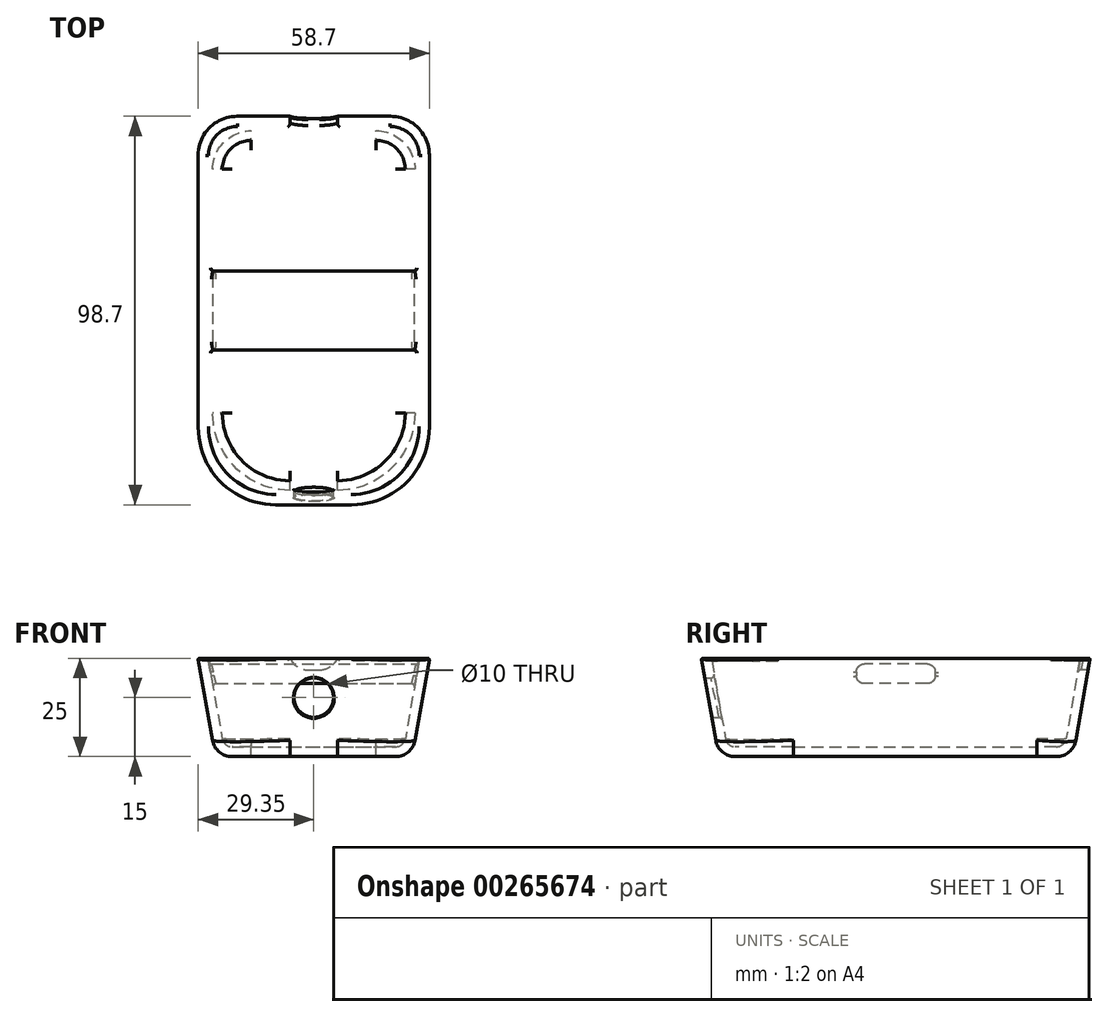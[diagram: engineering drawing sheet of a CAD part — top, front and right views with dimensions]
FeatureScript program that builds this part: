
annotation { "Feature Type Name" : "Feature", "Feature Type Description" : "" }
export const myFeature = defineFeature(function(context is Context, id is Id, definition is map)
    precondition{}
    {
        {
            var Q0;
            Q0=qCreatedBy(makeId("Top.planeOp"),FACE);
            var sketch = newSketch(context, id + "F0", { "sketchPlane" : qUnion([Q0])});
            skLineSegment(sketch, "E0.bottom", {"start": v(-25, 45) * mm, "end": v(25, 45) * mm});
            skLineSegment(sketch, "E0.top", {"start": v(-25, -45) * mm, "end": v(25, -45) * mm});
            skLineSegment(sketch, "E0.left", {"start": v(-25, 45) * mm, "end": v(-25, -45) * mm});
            skLineSegment(sketch, "E0.right", {"start": v(25, 45) * mm, "end": v(25, -45) * mm});
            skPoint(sketch, "E0.middle", {"position": v(0, 0) * mm});
            skSolve(sketch);
        }
        {
            var Q0;
            Q0=makeQuery(id+"F0.imprint","IMPRINT",FACE,{"disambiguationData":[TD([[makeQuery(id+"F0.imprint","IMPRINT",EDGE,{"derivedFrom":sQuery(id+"F0.wireOp",EDGE,"E0.bottom")}),-1.0]])]});
            extrude(context, id + "F1", {"entities" : qUnion([Q0]), "depth" : 25 * mm, "hasDraft" : true, "draftAngle" : 10 * degree});
        }
        {
            var Q0;
            Q0=makeQuery(id+"F1.opExtrude","SWEPT_EDGE",EDGE,{"disambiguationData":[OSD([sQuery(id+"F0.wireOp",EDGE,"E0.top"),sQuery(id+"F0.wireOp",EDGE,"E0.right")])]});
            var Q1;
            Q1=makeQuery(id+"F1.opExtrude","SWEPT_EDGE",EDGE,{"disambiguationData":[OSD([sQuery(id+"F0.wireOp",EDGE,"E0.top"),sQuery(id+"F0.wireOp",EDGE,"E0.left")])]});
            fillet(context, id + "F12", {"entities" : qUnion([Q0, Q1]), "radius" : 20 * mm, "tangentPropagation" : true, "allowEdgeOverflow" : false});
        }
        {
            var Q0;
            Q0=makeQuery(id+"F1.opExtrude","SWEPT_EDGE",EDGE,{"disambiguationData":[OSD([sQuery(id+"F0.wireOp",EDGE,"E0.bottom"),sQuery(id+"F0.wireOp",EDGE,"E0.left")])]});
            var Q1;
            Q1=makeQuery(id+"F1.opExtrude","SWEPT_EDGE",EDGE,{"disambiguationData":[OSD([sQuery(id+"F0.wireOp",EDGE,"E0.bottom"),sQuery(id+"F0.wireOp",EDGE,"E0.right")])]});
            fillet(context, id + "F2", {"entities" : qUnion([Q0, Q1]), "radius" : 10 * mm, "tangentPropagation" : true, "allowEdgeOverflow" : false});
        }
        {
            var Q0;
            Q0=makeQuery(id+"F1.opExtrude","CAP_EDGE",EDGE,{"disambiguationData":[OSD([sQuery(id+"F0.wireOp",EDGE,"E0.right")])],"isStart":true});
            var Q1;
            {var subQ0=sQuery(id+"F0.wireOp",EDGE,"E0.right");var subQ1=sQuery(id+"F0.wireOp",EDGE,"E0.bottom");Q1=makeQuery(id+"F2.opFillet","BLEND_EDGE",EDGE,{"blendedFrom":[makeQuery(id+"F1.opExtrude","SWEPT_EDGE",EDGE,{"disambiguationData":[OSD([subQ1,subQ0])]}),makeQuery(id+"F1.opExtrude","CAP_FACE",FACE,{"disambiguationData":[OSD([subQ1,sQuery(id+"F0.wireOp",EDGE,"E0.top"),sQuery(id+"F0.wireOp",EDGE,"E0.left"),subQ0])],"isStart":true})],"blendedInto":[makeQuery(id+"F1.opExtrude","CAP_FACE",FACE,{"disambiguationData":[OSD([subQ1,sQuery(id+"F0.wireOp",EDGE,"E0.top"),sQuery(id+"F0.wireOp",EDGE,"E0.left"),subQ0])],"isStart":true})]});}
            var Q2;
            Q2=makeQuery(id+"F1.opExtrude","CAP_EDGE",EDGE,{"disambiguationData":[OSD([sQuery(id+"F0.wireOp",EDGE,"E0.bottom")])],"isStart":true});
            var Q3;
            {var subQ0=sQuery(id+"F0.wireOp",EDGE,"E0.left");var subQ1=sQuery(id+"F0.wireOp",EDGE,"E0.bottom");Q3=makeQuery(id+"F2.opFillet","BLEND_EDGE",EDGE,{"blendedFrom":[makeQuery(id+"F1.opExtrude","SWEPT_EDGE",EDGE,{"disambiguationData":[OSD([subQ1,subQ0])]}),makeQuery(id+"F1.opExtrude","CAP_FACE",FACE,{"disambiguationData":[OSD([subQ1,sQuery(id+"F0.wireOp",EDGE,"E0.top"),subQ0,sQuery(id+"F0.wireOp",EDGE,"E0.right")])],"isStart":true})],"blendedInto":[makeQuery(id+"F1.opExtrude","CAP_FACE",FACE,{"disambiguationData":[OSD([subQ1,sQuery(id+"F0.wireOp",EDGE,"E0.top"),subQ0,sQuery(id+"F0.wireOp",EDGE,"E0.right")])],"isStart":true})]});}
            var Q4;
            Q4=makeQuery(id+"F1.opExtrude","CAP_EDGE",EDGE,{"disambiguationData":[OSD([sQuery(id+"F0.wireOp",EDGE,"E0.left")])],"isStart":true});
            var Q5;
            {var subQ0=sQuery(id+"F0.wireOp",EDGE,"E0.left");var subQ1=sQuery(id+"F0.wireOp",EDGE,"E0.top");Q5=makeQuery(id+"F12.opFillet","BLEND_EDGE",EDGE,{"blendedFrom":[makeQuery(id+"F1.opExtrude","SWEPT_EDGE",EDGE,{"disambiguationData":[OSD([subQ1,subQ0])]}),makeQuery(id+"F1.opExtrude","CAP_FACE",FACE,{"disambiguationData":[OSD([sQuery(id+"F0.wireOp",EDGE,"E0.bottom"),subQ1,subQ0,sQuery(id+"F0.wireOp",EDGE,"E0.right")])],"isStart":true})],"blendedInto":[makeQuery(id+"F1.opExtrude","CAP_FACE",FACE,{"disambiguationData":[OSD([sQuery(id+"F0.wireOp",EDGE,"E0.bottom"),subQ1,subQ0,sQuery(id+"F0.wireOp",EDGE,"E0.right")])],"isStart":true})]});}
            var Q6;
            {var subQ0=sQuery(id+"F0.wireOp",EDGE,"E0.right");var subQ1=sQuery(id+"F0.wireOp",EDGE,"E0.top");Q6=makeQuery(id+"F12.opFillet","BLEND_EDGE",EDGE,{"blendedFrom":[makeQuery(id+"F1.opExtrude","SWEPT_EDGE",EDGE,{"disambiguationData":[OSD([subQ1,subQ0])]}),makeQuery(id+"F1.opExtrude","CAP_FACE",FACE,{"disambiguationData":[OSD([sQuery(id+"F0.wireOp",EDGE,"E0.bottom"),subQ1,sQuery(id+"F0.wireOp",EDGE,"E0.left"),subQ0])],"isStart":true})],"blendedInto":[makeQuery(id+"F1.opExtrude","CAP_FACE",FACE,{"disambiguationData":[OSD([sQuery(id+"F0.wireOp",EDGE,"E0.bottom"),subQ1,sQuery(id+"F0.wireOp",EDGE,"E0.left"),subQ0])],"isStart":true})]});}
            var Q7;
            Q7=makeQuery(id+"F1.opExtrude","CAP_EDGE",EDGE,{"disambiguationData":[OSD([sQuery(id+"F0.wireOp",EDGE,"E0.top")])],"isStart":true});
            fillet(context, id + "F3", {"entities" : qUnion([Q0, Q1, Q2, Q3, Q4, Q5, Q6, Q7]), "radius" : 5 * mm, "tangentPropagation" : true, "allowEdgeOverflow" : false});
        }
        {
            var Q0;
            Q0=makeQuery(id+"F1.opExtrude","CAP_FACE",FACE,{"disambiguationData":[OSD([sQuery(id+"F0.wireOp",EDGE,"E0.bottom"),sQuery(id+"F0.wireOp",EDGE,"E0.top"),sQuery(id+"F0.wireOp",EDGE,"E0.left"),sQuery(id+"F0.wireOp",EDGE,"E0.right")])],"isStart":false});
            shell(context, id + "F4", {"entities" : qUnion([Q0]), "thickness" : 2.5 * mm});
        }
        {
            var Q0;
            Q0=qCreatedBy(makeId("Front.planeOp"),FACE);
            var sketch = newSketch(context, id + "F5", { "sketchPlane" : qUnion([Q0])});
            skLineSegment(sketch, "E1", {"start": v(0, 0) * mm, "end": v(0, 25) * mm, "construction": true});
            skLineSegment(sketch, "E2.bottom", {"start": v(9.5, 33.44) * mm, "end": v(10.2, 33.44) * mm});
            skLineSegment(sketch, "E2.top", {"start": v(9.5, 33.72) * mm, "end": v(10.2, 33.72) * mm});
            skLineSegment(sketch, "E2.left", {"start": v(9.5, 33.44) * mm, "end": v(9.5, 33.72) * mm});
            skLineSegment(sketch, "E2.right", {"start": v(10.2, 33.44) * mm, "end": v(10.2, 33.72) * mm});
            skPoint(sketch, "E2.middle", {"position": v(9.85, 33.58) * mm});
            skLineSegment(sketch, "E3.bottom", {"start": v(6, 28) * mm, "end": v(-6, 28) * mm});
            skLineSegment(sketch, "E3.top", {"start": v(6, 22) * mm, "end": v(-6, 22) * mm});
            skLineSegment(sketch, "E3.left", {"start": v(6, 28) * mm, "end": v(6, 22) * mm});
            skLineSegment(sketch, "E3.right", {"start": v(-6, 28) * mm, "end": v(-6, 22) * mm});
            skPoint(sketch, "E3.middle", {"position": v(0, 25) * mm});
            skSolve(sketch);
        }
        {
            var Q0;
            Q0=makeQuery(id+"F5.imprint","IMPRINT",FACE,{"disambiguationData":[TD([[makeQuery(id+"F5.imprint","IMPRINT",EDGE,{"derivedFrom":sQuery(id+"F5.wireOp",EDGE,"E3.bottom")}),1.0]])]});
            extrude(context, id + "F13", {"entities" : qUnion([Q0]), "operationType" : NewBodyOperationType.REMOVE, "oppositeDirection" : true, "depth" : 60 * mm});
        }
        {
            var Q0;
            Q0=qCreatedBy(makeId("Front.planeOp"),FACE);
            var sketch = newSketch(context, id + "F6", { "sketchPlane" : qUnion([Q0])});
            skCircle(sketch, "E4", {"center": v(0, 15) * mm, "radius": 5 * mm});
            skSolve(sketch);
        }
        {
            var Q0;
            Q0=makeQuery(id+"F6.imprint","IMPRINT",FACE,{"disambiguationData":[TD([[makeQuery(id+"F6.imprint","IMPRINT",EDGE,{"derivedFrom":sQuery(id+"F6.wireOp",EDGE,"E4")}),1.0]])]});
            extrude(context, id + "F14", {"entities" : qUnion([Q0]), "operationType" : NewBodyOperationType.REMOVE, "depth" : 50 * mm});
        }
        {
            var Q0;
            {var subQ0=sQuery(id+"F0.wireOp",EDGE,"E0.right");var subQ1=sQuery(id+"F0.wireOp",EDGE,"E0.left");var subQ2=sQuery(id+"F0.wireOp",EDGE,"E0.top");var subQ3=sQuery(id+"F0.wireOp",EDGE,"E0.bottom");Q0=makeQuery(id+"F4.opShell","OFFSET_FACE",FACE,{"disambiguationData":[OSD([subQ3,subQ2,subQ1,subQ0]),TDD([makeQuery(id+"F1.opExtrude","CAP_FACE",FACE,{"disambiguationData":[OSD([subQ3,subQ2,subQ1,subQ0])],"isStart":true})])]});}
            var sketch = newSketch(context, id + "F15", { "sketchPlane" : qUnion([Q0])});
            skLineSegment(sketch, "E5", {"start": v(0, 0) * mm, "end": v(0, 35) * mm, "construction": true});
            skLineSegment(sketch, "E6", {"start": v(0, 35) * mm, "end": v(-15, 35) * mm, "construction": true});
            skSolve(sketch);
        }
        {
            var Q0;
            {var subQ0=sQuery(id+"F0.wireOp",EDGE,"E0.right");var subQ1=sQuery(id+"F0.wireOp",EDGE,"E0.left");var subQ2=sQuery(id+"F0.wireOp",EDGE,"E0.top");var subQ3=sQuery(id+"F0.wireOp",EDGE,"E0.bottom");var subQ4=makeQuery(id+"F1.opExtrude","CAP_FACE",FACE,{"disambiguationData":[OSD([subQ3,subQ2,subQ1,subQ0])],"isStart":true});var subQ5=subQ4;var subQ6=subQ5;Q0=makeQuery(id+"F15.imprint","IMPRINT",FACE,{"disambiguationData":[TD([[makeQuery(id+"F15.imprint","IMPRINT",EDGE,{"derivedFrom":makeQuery(id+"F4.opShell","OFFSET_EDGE",EDGE,{"disambiguationData":[OSD([subQ3,subQ2,subQ1,subQ0]),TDD([makeQuery(id+"F3.opFillet","BLEND_EDGE",EDGE,{"blendedFrom":[makeQuery(id+"F1.opExtrude","CAP_EDGE",EDGE,{"disambiguationData":[OSD([subQ2])],"isStart":true}),subQ6],"blendedInto":[subQ6]})])]})}),-1.0]])]});}
            var sketch = newSketch(context, id + "F16", { "sketchPlane" : qUnion([Q0])});
            skCircle(sketch, "E7", {"center": v(-14.97, 34.98) * mm, "radius": 4 * mm});
            skCircle(sketch, "E8", {"center": v(-14.97, 34.98) * mm, "radius": 2.5 * mm});
            skSolve(sketch);
        }
        {
            var Q0;
            Q0=makeQuery(id+"F16.imprint","IMPRINT",FACE,{"disambiguationData":[TD([[makeQuery(id+"F16.imprint","IMPRINT",EDGE,{"derivedFrom":sQuery(id+"F16.wireOp",EDGE,"E7")}),1.0]])]});
            extrude(context, id + "F17", {"entities" : qUnion([Q0]), "depth" : 10 * mm, "hasDraft" : true, "draftAngle" : 1.5 * degree, "draftPullDirection" : true});
        }
        {
            var Q0;
            Q0=makeQuery(id+"F17.opExtrude","CAP_EDGE",EDGE,{"disambiguationData":[OSD([sQuery(id+"F16.wireOp",EDGE,"E7")])],"isStart":false});
            fillet(context, id + "F7", {"entities" : qUnion([Q0]), "radius" : 1 * mm, "tangentPropagation" : true, "allowEdgeOverflow" : false});
        }
        {
            var Q0;
            Q0=makeQuery(id+"F17.opExtrude","CAP_EDGE",EDGE,{"disambiguationData":[OSD([sQuery(id+"F16.wireOp",EDGE,"E7")])],"isStart":true});
            fillet(context, id + "F18", {"entities" : qUnion([Q0]), "radius" : 2 * mm, "tangentPropagation" : true, "allowEdgeOverflow" : false});
        }
        {
            var Q0;
            Q0=makeQuery(id+"F17.opExtrude","SWEPT_BODY",BODY,{"disambiguationData":[OSD([sQuery(id+"F16.wireOp",EDGE,"E7"),sQuery(id+"F16.wireOp",EDGE,"E8")])]});
            deleteBodies(context, id + "F19", {"entities" : qUnion([Q0])});
        }
        {
            var Q0;
            Q0=qCreatedBy(makeId("Right.planeOp"),FACE);
            var sketch = newSketch(context, id + "F8", { "sketchPlane" : qUnion([Q0])});
            skLineSegment(sketch, "E9.bottom", {"start": v(10, 23.56) * mm, "end": v(-10, 23.56) * mm});
            skLineSegment(sketch, "E9.top", {"start": v(10, 18.56) * mm, "end": v(-10, 18.56) * mm});
            skLineSegment(sketch, "E9.left", {"start": v(10, 23.56) * mm, "end": v(10, 18.56) * mm});
            skLineSegment(sketch, "E9.right", {"start": v(-10, 23.56) * mm, "end": v(-10, 18.56) * mm});
            skPoint(sketch, "E9.middle", {"position": v(0, 21.06) * mm});
            skSolve(sketch);
        }
        {
            var Q0;
            Q0=makeQuery(id+"F8.imprint","IMPRINT",FACE,{"disambiguationData":[TD([[makeQuery(id+"F8.imprint","IMPRINT",EDGE,{"derivedFrom":sQuery(id+"F8.wireOp",EDGE,"E9.bottom")}),1.0]])]});
            extrude(context, id + "F9", {"entities" : qUnion([Q0]), "operationType" : NewBodyOperationType.ADD, "endBound" : BoundingType.SYMMETRIC, "oppositeDirection" : true, "depth" : 56 * mm});
        }
        {
            var Q0;
            Q0=makeQuery(id+"F9.opExtrude","SWEPT_EDGE",EDGE,{"disambiguationData":[OSD([sQuery(id+"F8.wireOp",EDGE,"E9.bottom"),sQuery(id+"F8.wireOp",EDGE,"E9.right")])]});
            var Q1;
            Q1=makeQuery(id+"F9.opExtrude","SWEPT_EDGE",EDGE,{"disambiguationData":[OSD([sQuery(id+"F8.wireOp",EDGE,"E9.top"),sQuery(id+"F8.wireOp",EDGE,"E9.right")])]});
            var Q2;
            Q2=makeQuery(id+"F9.opExtrude","SWEPT_EDGE",EDGE,{"disambiguationData":[OSD([sQuery(id+"F8.wireOp",EDGE,"E9.bottom"),sQuery(id+"F8.wireOp",EDGE,"E9.left")])]});
            var Q3;
            Q3=makeQuery(id+"F9.opExtrude","SWEPT_EDGE",EDGE,{"disambiguationData":[OSD([sQuery(id+"F8.wireOp",EDGE,"E9.top"),sQuery(id+"F8.wireOp",EDGE,"E9.left")])]});
            fillet(context, id + "F20", {"entities" : qUnion([Q0, Q1, Q2, Q3]), "radius" : 2 * mm, "tangentPropagation" : true, "allowEdgeOverflow" : false});
        }
        {
            var Q0;
            Q0=makeQuery(id+"F13.boolean.opBoolean","COPY",EDGE,{"derivedFrom":makeQuery(id+"F13.opExtrude","SWEPT_EDGE",EDGE,{"disambiguationData":[OSD([sQuery(id+"F5.wireOp",EDGE,"E3.top"),sQuery(id+"F5.wireOp",EDGE,"E3.left")])]})});
            var Q1;
            Q1=makeQuery(id+"F13.boolean.opBoolean","COPY",EDGE,{"derivedFrom":makeQuery(id+"F13.opExtrude","SWEPT_EDGE",EDGE,{"disambiguationData":[OSD([sQuery(id+"F5.wireOp",EDGE,"E3.top"),sQuery(id+"F5.wireOp",EDGE,"E3.right")])]})});
            fillet(context, id + "F10", {"entities" : qUnion([Q0, Q1]), "radius" : 5 * mm, "tangentPropagation" : true, "allowEdgeOverflow" : false});
        }
        {
            var Q0;
            {var subQ0=sQuery(id+"F0.wireOp",EDGE,"E0.left");Q0=makeQuery(id+"F4.opShell","OFFSET_FACE",FACE,{"disambiguationData":[OSD([subQ0]),TDD([makeQuery(id+"F1.opExtrude","SWEPT_FACE",FACE,{"disambiguationData":[OSD([subQ0])]})])]});}
            var Q1;
            Q1=makeQuery(id+"F4.opShell","OFFSET_FACE",FACE,{"disambiguationData":[OSD([sQuery(id+"F0.wireOp",EDGE,"E0.bottom"),sQuery(id+"F0.wireOp",EDGE,"E0.left")])]});
            var Q2;
            {var subQ0=sQuery(id+"F0.wireOp",EDGE,"E0.bottom");Q2=makeQuery(id+"F4.opShell","OFFSET_FACE",FACE,{"disambiguationData":[OSD([subQ0]),TDD([makeQuery(id+"F1.opExtrude","SWEPT_FACE",FACE,{"disambiguationData":[OSD([subQ0])]})])]});}
            var Q3;
            {var subQ0=sQuery(id+"F0.wireOp",EDGE,"E0.right");Q3=makeQuery(id+"F4.opShell","OFFSET_FACE",FACE,{"disambiguationData":[OSD([subQ0]),TDD([makeQuery(id+"F1.opExtrude","SWEPT_FACE",FACE,{"disambiguationData":[OSD([subQ0])]})])]});}
            var Q4;
            Q4=makeQuery(id+"F4.opShell","OFFSET_FACE",FACE,{"disambiguationData":[OSD([sQuery(id+"F0.wireOp",EDGE,"E0.bottom"),sQuery(id+"F0.wireOp",EDGE,"E0.right")])]});
            var Q5;
            Q5=makeQuery(id+"F4.opShell","OFFSET_FACE",FACE,{"disambiguationData":[OSD([sQuery(id+"F0.wireOp",EDGE,"E0.top"),sQuery(id+"F0.wireOp",EDGE,"E0.right")])]});
            var Q6;
            {var subQ0=sQuery(id+"F0.wireOp",EDGE,"E0.top");Q6=makeQuery(id+"F4.opShell","OFFSET_FACE",FACE,{"disambiguationData":[OSD([subQ0]),TDD([makeQuery(id+"F1.opExtrude","SWEPT_FACE",FACE,{"disambiguationData":[OSD([subQ0])]})])]});}
            var Q7;
            Q7=makeQuery(id+"F4.opShell","OFFSET_FACE",FACE,{"disambiguationData":[OSD([sQuery(id+"F0.wireOp",EDGE,"E0.top"),sQuery(id+"F0.wireOp",EDGE,"E0.left")])]});
            fillet(context, id + "F21", {"entities" : qUnion([Q0, Q1, Q2, Q3, Q4, Q5, Q6, Q7]), "radius" : 0.8 * mm, "tangentPropagation" : true, "allowEdgeOverflow" : false});
        }
        {
            var Q0;
            Q0=makeQuery(id+"F1.opExtrude","SWEPT_FACE",FACE,{"disambiguationData":[OSD([sQuery(id+"F0.wireOp",EDGE,"E0.top")])]});
            var Q1;
            Q1=makeQuery(id+"F12.opFillet","BLEND_FACE",FACE,{"disambiguationData":[OSD([sQuery(id+"F0.wireOp",EDGE,"E0.top"),sQuery(id+"F0.wireOp",EDGE,"E0.right")])]});
            var Q2;
            Q2=makeQuery(id+"F1.opExtrude","SWEPT_FACE",FACE,{"disambiguationData":[OSD([sQuery(id+"F0.wireOp",EDGE,"E0.right")])]});
            var Q3;
            Q3=makeQuery(id+"F12.opFillet","BLEND_FACE",FACE,{"disambiguationData":[OSD([sQuery(id+"F0.wireOp",EDGE,"E0.top"),sQuery(id+"F0.wireOp",EDGE,"E0.left")])]});
            var Q4;
            Q4=makeQuery(id+"F1.opExtrude","SWEPT_FACE",FACE,{"disambiguationData":[OSD([sQuery(id+"F0.wireOp",EDGE,"E0.left")])]});
            var Q5;
            Q5=makeQuery(id+"F2.opFillet","BLEND_FACE",FACE,{"disambiguationData":[OSD([sQuery(id+"F0.wireOp",EDGE,"E0.bottom"),sQuery(id+"F0.wireOp",EDGE,"E0.left")])]});
            var Q6;
            Q6=makeQuery(id+"F1.opExtrude","SWEPT_FACE",FACE,{"disambiguationData":[OSD([sQuery(id+"F0.wireOp",EDGE,"E0.bottom")])]});
            var Q7;
            Q7=makeQuery(id+"F2.opFillet","BLEND_FACE",FACE,{"disambiguationData":[OSD([sQuery(id+"F0.wireOp",EDGE,"E0.bottom"),sQuery(id+"F0.wireOp",EDGE,"E0.right")])]});
            fillet(context, id + "F11", {"entities" : qUnion([Q0, Q1, Q2, Q3, Q4, Q5, Q6, Q7]), "radius" : 0.3 * mm, "tangentPropagation" : true, "allowEdgeOverflow" : false});
        }
    });
